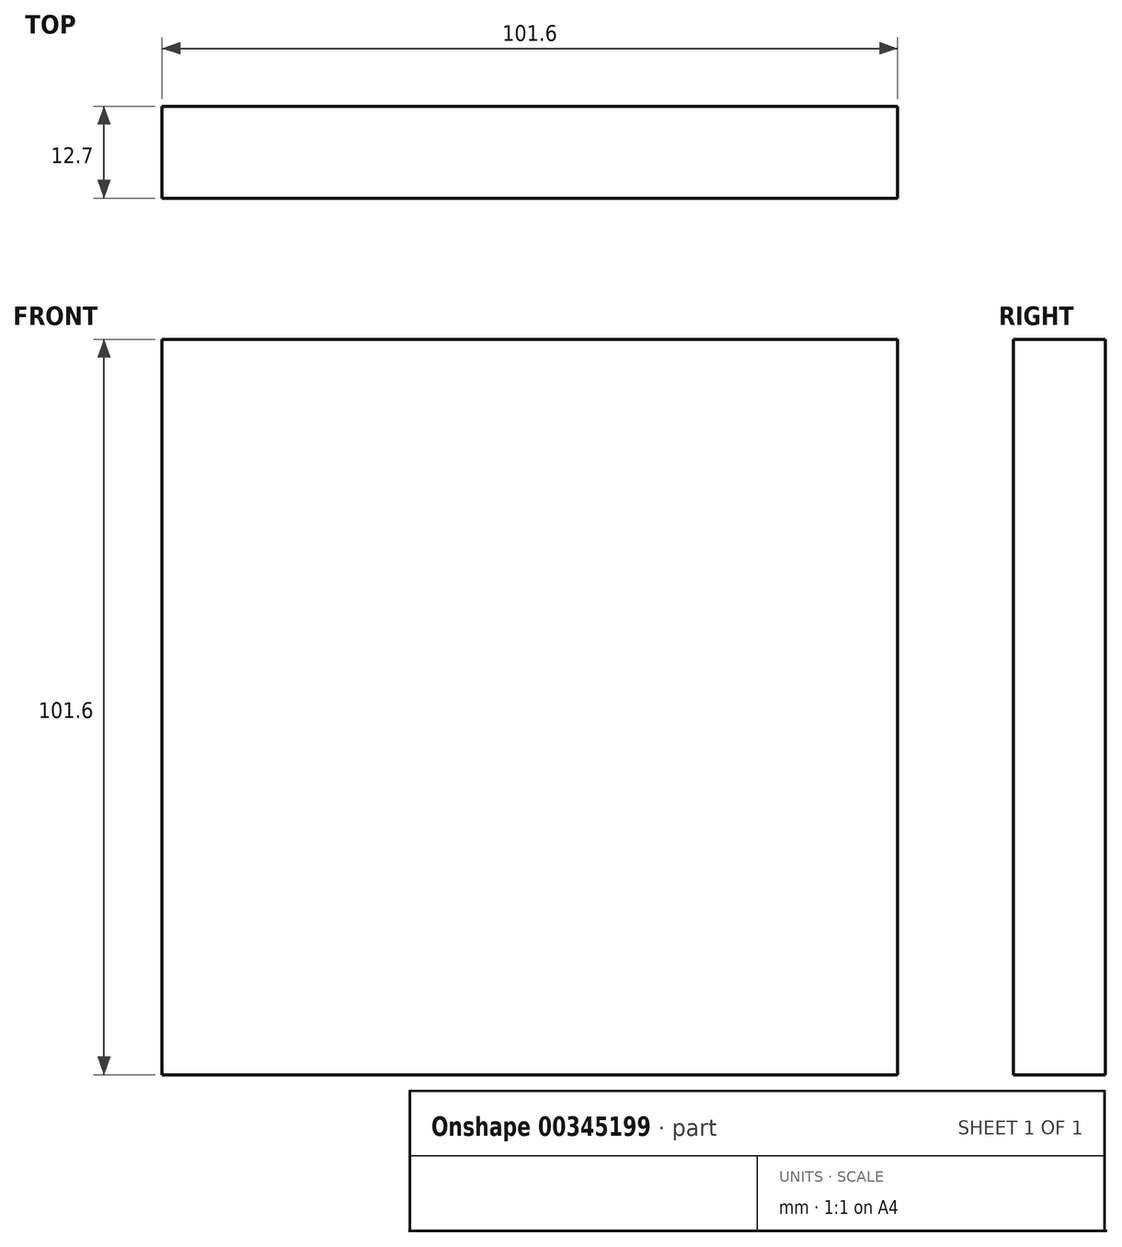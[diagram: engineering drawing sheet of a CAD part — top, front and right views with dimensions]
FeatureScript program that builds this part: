
annotation { "Feature Type Name" : "Feature", "Feature Type Description" : "" }
export const myFeature = defineFeature(function(context is Context, id is Id, definition is map)
    precondition{}
    {
        {
            var Q0;
            Q0=qCreatedBy(makeId("Front.planeOp"),FACE);
            var sketch = newSketch(context, id + "F0", { "sketchPlane" : qUnion([Q0])});
            skLineSegment(sketch, "E0.bottom", {"start": v(50.8, 50.8) * mm, "end": v(-50.8, 50.8) * mm});
            skLineSegment(sketch, "E0.top", {"start": v(50.8, -50.8) * mm, "end": v(-50.8, -50.8) * mm});
            skLineSegment(sketch, "E0.left", {"start": v(50.8, 50.8) * mm, "end": v(50.8, -50.8) * mm});
            skLineSegment(sketch, "E0.right", {"start": v(-50.8, 50.8) * mm, "end": v(-50.8, -50.8) * mm});
            skPoint(sketch, "E0.middle", {"position": v(0, 0) * mm});
            skSolve(sketch);
        }
        {
            var Q0;
            Q0=makeQuery(id+"F0.imprint","IMPRINT",FACE,{"disambiguationData":[TD([[makeQuery(id+"F0.imprint","IMPRINT",EDGE,{"derivedFrom":sQuery(id+"F0.wireOp",EDGE,"E0.bottom")}),1.0]])]});
            extrude(context, id + "F1", {"entities" : qUnion([Q0]), "endBound" : BoundingType.SYMMETRIC, "oppositeDirection" : true, "depth" : 12.7 * mm});
        }
    });
